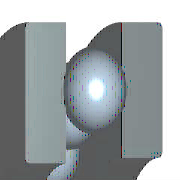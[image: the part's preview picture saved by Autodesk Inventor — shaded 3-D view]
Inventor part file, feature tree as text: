
AUTODESK INVENTOR PART (.ipt)
format: ipt  version: 2022 (Build 260153000, 153)  size: 317,952 bytes
history: native  units: mm (DEFAULTED — no unit token found)
features: sketch x1, other x1, pattern_circular x1
ambient origin geometry x8: Origin, YZ Plane, XZ Plane, XY Plane, X Axis, Y Axis, Z Axis, Center Point
bodies: Solid1 (feature_tree), Body (feature_tree)
feature tree (3):
  sketch  "Sketch"  dims[d0=2.8mm d9=90.0deg d10=90.0deg d1=160.0mm d2=360.0deg d3=6.16mm d4=0.6mm d5=0.6mm d6=0.0mm d7=0.0mm d8=50.0mm d11=52.0mm d12=61.0mm d13=70.0mm d14=70.0mm d15=7.0mm d16=14.0mm d18=4.2mm d19=0.0mm d46=0.0mm d47=0.0mm]
  other  "Ball"
  pattern_circular  "Balls"  Angle=90.0deg  [1 undecoded]
note: 1 required parameter value undecoded (feature->parameter linkage not recoverable at this tier; creation-order binding heuristic only, values carry confidence <= 0.55)
